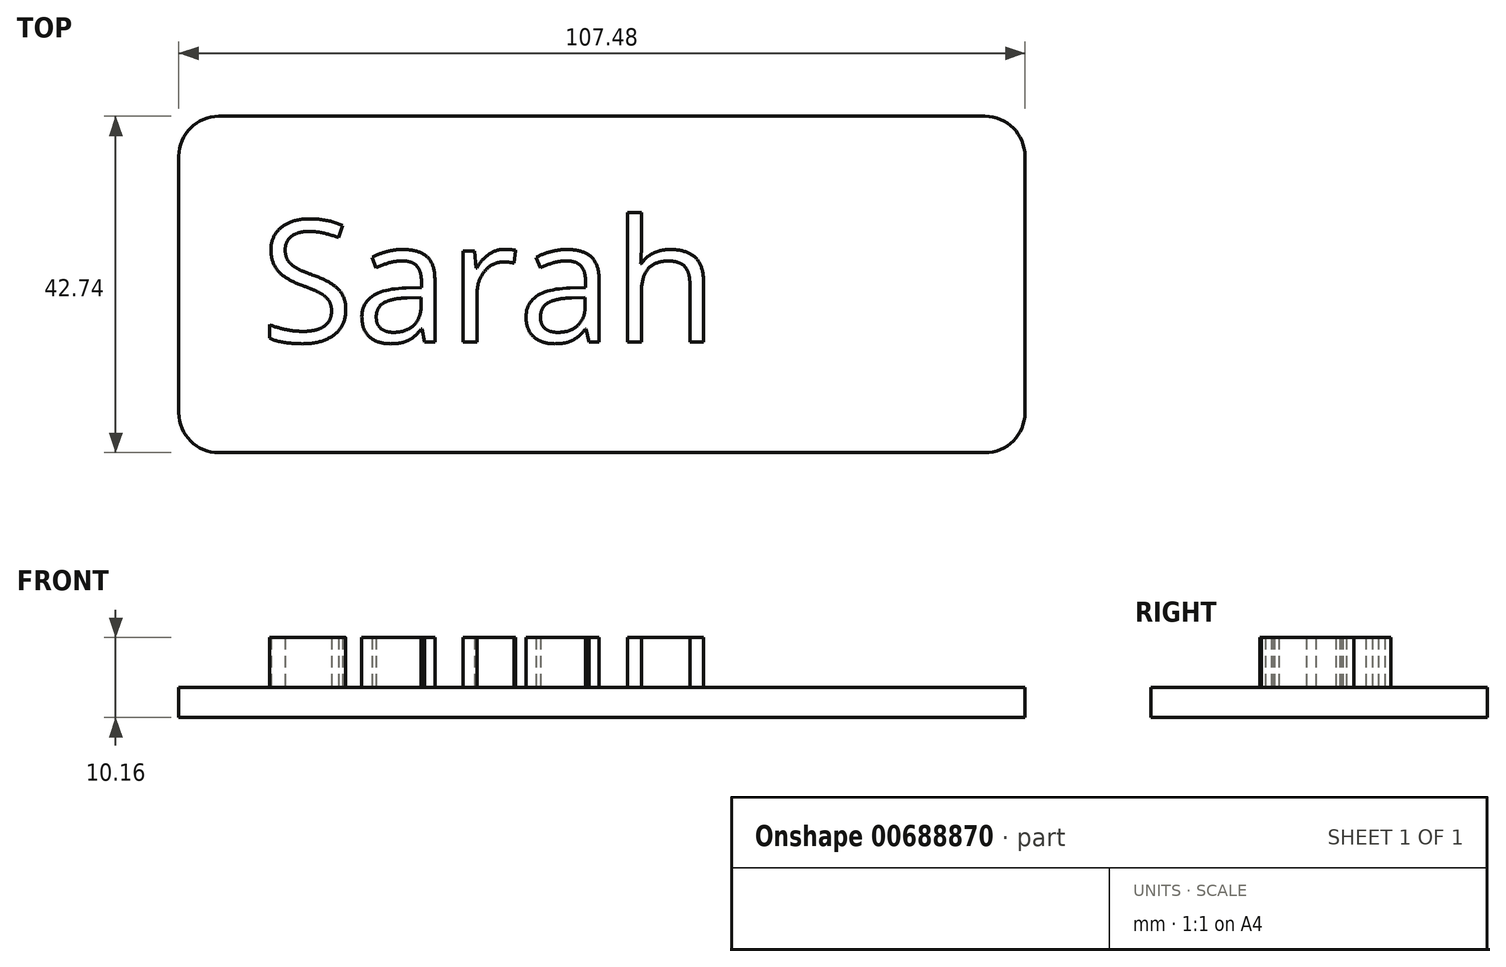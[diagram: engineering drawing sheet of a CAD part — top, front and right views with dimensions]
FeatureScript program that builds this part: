
annotation { "Feature Type Name" : "Feature", "Feature Type Description" : "" }
export const myFeature = defineFeature(function(context is Context, id is Id, definition is map)
    precondition{}
    {
        {
            var Q0;
            Q0=qCreatedBy(makeId("Top.planeOp"),FACE);
            var sketch = newSketch(context, id + "F0", { "sketchPlane" : qUnion([Q0])});
            skLineSegment(sketch, "E0.bottom", {"start": v(-49.93, -35.58) * mm, "end": v(57.55, -35.58) * mm});
            skLineSegment(sketch, "E0.top", {"start": v(-49.93, 7.16) * mm, "end": v(57.55, 7.16) * mm});
            skLineSegment(sketch, "E0.left", {"start": v(-49.93, -35.58) * mm, "end": v(-49.93, 7.16) * mm});
            skLineSegment(sketch, "E0.right", {"start": v(57.55, -35.58) * mm, "end": v(57.55, 7.16) * mm});
            skSolve(sketch);
        }
        {
            var Q0;
            Q0 = qSketchRegion(id + "F0", true);
            extrude(context, id + "F1", {"entities" : qUnion([Q0]), "depth" : 3.8 * mm, "offsetDistance" : 25.4 * mm});
        }
        {
            var Q0;
            Q0=makeQuery(id+"F1.opExtrude","SWEPT_EDGE",EDGE,{"disambiguationData":[OSD([sQuery(id+"F0.wireOp",EDGE,"E0.bottom"),sQuery(id+"F0.wireOp",EDGE,"E0.right")])]});
            fillet(context, id + "F2", {"entities" : qUnion([Q0]), "radius" : 5.08 * mm, "tangentPropagation" : true, "allowEdgeOverflow" : false});
        }
        {
            var Q0;
            Q0=makeQuery(id+"F1.opExtrude","SWEPT_EDGE",EDGE,{"disambiguationData":[OSD([sQuery(id+"F0.wireOp",EDGE,"E0.top"),sQuery(id+"F0.wireOp",EDGE,"E0.right")])]});
            fillet(context, id + "F3", {"entities" : qUnion([Q0]), "radius" : 5.08 * mm, "tangentPropagation" : true, "allowEdgeOverflow" : false});
        }
        {
            var Q0;
            Q0=makeQuery(id+"F1.opExtrude","SWEPT_EDGE",EDGE,{"disambiguationData":[OSD([sQuery(id+"F0.wireOp",EDGE,"E0.top"),sQuery(id+"F0.wireOp",EDGE,"E0.left")])]});
            fillet(context, id + "F4", {"entities" : qUnion([Q0]), "radius" : 5.08 * mm, "tangentPropagation" : true, "allowEdgeOverflow" : false});
        }
        {
            var Q0;
            Q0=makeQuery(id+"F1.opExtrude","SWEPT_EDGE",EDGE,{"disambiguationData":[OSD([sQuery(id+"F0.wireOp",EDGE,"E0.bottom"),sQuery(id+"F0.wireOp",EDGE,"E0.left")])]});
            fillet(context, id + "F5", {"entities" : qUnion([Q0]), "radius" : 5.08 * mm, "tangentPropagation" : true, "allowEdgeOverflow" : false});
        }
        {
            var Q0;
            Q0=makeQuery(id+"F1.opExtrude","CAP_FACE",FACE,{"disambiguationData":[OSD([sQuery(id+"F0.wireOp",EDGE,"E0.bottom"),sQuery(id+"F0.wireOp",EDGE,"E0.top"),sQuery(id+"F0.wireOp",EDGE,"E0.left"),sQuery(id+"F0.wireOp",EDGE,"E0.right")])],"isStart":false});
            var sketch = newSketch(context, id + "F6", { "sketchPlane" : qUnion([Q0])});
            skText(sketch, "E1", { "text": "Sarah", "fontName": "OpenSans-Regular.ttf"});
            const initialGuessF6  = {"E1": [-0.03955, -0.02153, 1, 0, 0.01557]};
            skSetInitialGuess(sketch, initialGuessF6);
            skSolve(sketch);
        }
        {
            var Q0;
            Q0 = qSketchRegion(id + "F6", true);
            extrude(context, id + "F7", {"entities" : qUnion([Q0]), "operationType" : NewBodyOperationType.ADD, "depth" : 6.35 * mm, "offsetDistance" : 25.4 * mm});
        }
    });
